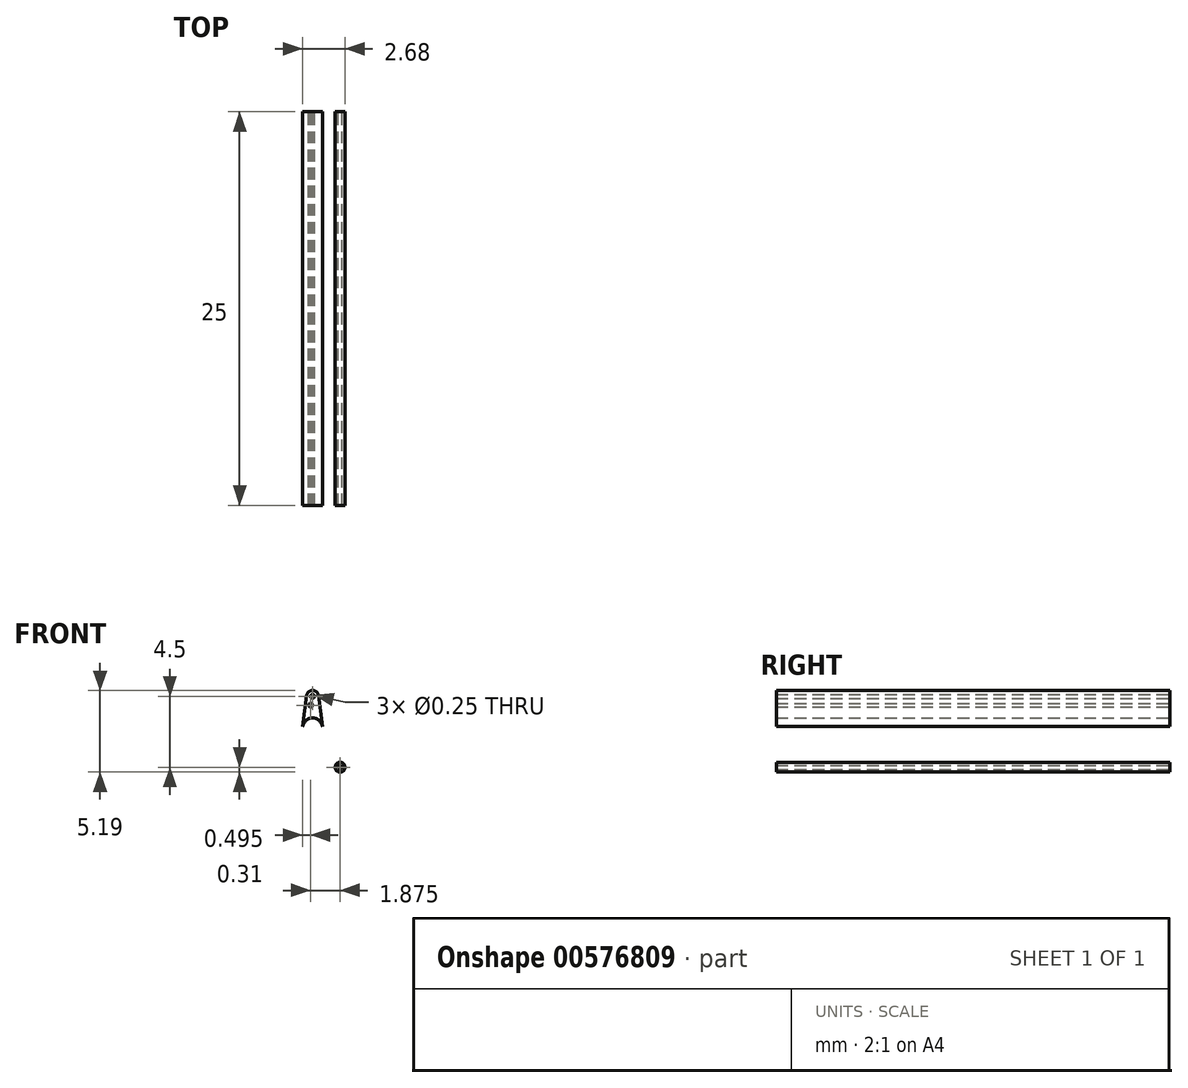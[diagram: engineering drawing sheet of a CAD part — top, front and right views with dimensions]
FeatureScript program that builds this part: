
annotation { "Feature Type Name" : "Feature", "Feature Type Description" : "" }
export const myFeature = defineFeature(function(context is Context, id is Id, definition is map)
    precondition{}
    {
        {
            var Q0;
            Q0=qCreatedBy(makeId("Front.planeOp"),FACE);
            var sketch = newSketch(context, id + "F0", { "sketchPlane" : qUnion([Q0])});
            skLineSegment(sketch, "E0", {"start": v(0, 0) * mm, "end": v(0, 4.5) * mm, "construction": true});
            skLineSegment(sketch, "E1", {"start": v(0, 0) * mm, "end": v(1.75, 0) * mm, "construction": true});
            skCircle(sketch, "E2", {"center": v(0, 4.5) * mm, "radius": 0.38 * mm});
            skCircle(sketch, "E3", {"center": v(0, 2.5) * mm, "radius": 0.62 * mm});
            skCircle(sketch, "E4", {"center": v(0, 0) * mm, "radius": 0.38 * mm});
            skCircle(sketch, "E5", {"center": v(1.75, 0) * mm, "radius": 0.31 * mm});
            skLineSegment(sketch, "E6", {"start": v(-0.62, 2.58) * mm, "end": v(-0.37, 4.55) * mm});
            skLineSegment(sketch, "E7", {"start": v(0.62, 2.58) * mm, "end": v(0.37, 4.55) * mm});
            skPoint(sketch, "E8.startSnap0", {"position": v(0, 2.25) * mm});
            skLineSegment(sketch, "E9", {"start": v(0.75, 0.35) * mm, "end": v(1.76, 0.31) * mm});
            skLineSegment(sketch, "E10", {"start": v(0.01, -0.37) * mm, "end": v(1.76, -0.31) * mm});
            skLineSegment(sketch, "E11", {"start": v(-0.37, -0.04) * mm, "end": v(-0.62, 2.44) * mm});
            skCircle(sketch, "E12", {"center": v(0, 4.5) * mm, "radius": 0.12 * mm});
            skCircle(sketch, "E13", {"center": v(0, 2.5) * mm, "radius": 0.12 * mm});
            skCircle(sketch, "E14", {"center": v(0, 0) * mm, "radius": 0.12 * mm});
            skCircle(sketch, "E15", {"center": v(1.75, 0) * mm, "radius": 0.12 * mm});
            skCircle(sketch, "E16", {"center": v(-0.12, 3.94) * mm, "radius": 0.12 * mm});
            skLineSegment(sketch, "E17", {"start": v(0.62, 2.44) * mm, "end": v(0.45, 0.7) * mm});
            skArc(sketch, "E18.filletArc", {"start": v(0.45, 0.7) * mm, "mid": v(0.52, 0.46) * mm, "end": v(0.75, 0.35) * mm});
            skSolve(sketch);
        }
        {
            var Q0;
            Q0=makeQuery(id+"F0.imprint","IMPRINT",FACE,{"disambiguationData":[TD([[makeQuery(id+"F0.imprint","IMPRINT",EDGE,{"derivedFrom":sQuery(id+"F0.wireOp",EDGE,"E12")}),-1.0]])]});
            var Q1;
            {var subQ0=sQuery(id+"F0.wireOp",EDGE,"E6");Q1=makeQuery(id+"F0.imprint","IMPRINT",FACE,{"disambiguationData":[TD([[makeQuery(id+"F0.imprint","IMPRINT",EDGE,{"derivedFrom":subQ0}),-1.0]])]});}
            var Q2;
            Q2=makeQuery(id+"F0.imprint","IMPRINT",FACE,{"disambiguationData":[TD([[makeQuery(id+"F0.imprint","IMPRINT",EDGE,{"derivedFrom":sQuery(id+"F0.wireOp",EDGE,"E15")}),-1.0]])]});
            extrude(context, id + "F1", {"entities" : qUnion([Q0, Q1, Q2]), "depth" : 25 * mm, "offsetDistance" : 25 * mm});
        }
    });
